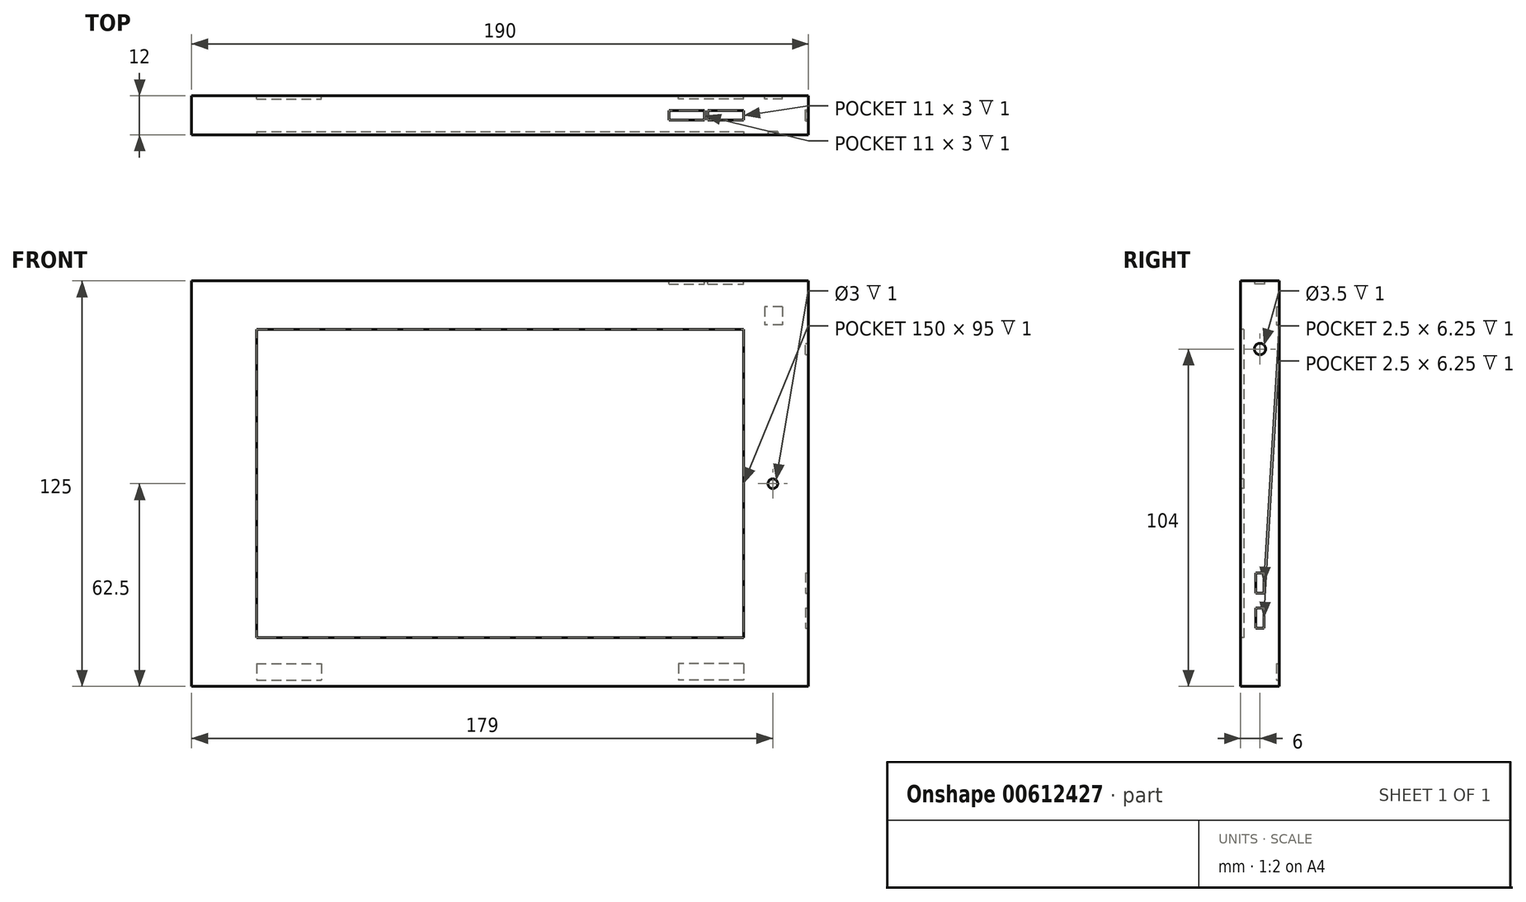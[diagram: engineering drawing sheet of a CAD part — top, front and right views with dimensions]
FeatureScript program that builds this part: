
annotation { "Feature Type Name" : "Feature", "Feature Type Description" : "" }
export const myFeature = defineFeature(function(context is Context, id is Id, definition is map)
    precondition{}
    {
        {
            var Q0;
            Q0=qCreatedBy(makeId("Right.planeOp"),FACE);
            var sketch = newSketch(context, id + "F0", { "sketchPlane" : qUnion([Q0])});
            skLineSegment(sketch, "E0.bottom", {"start": v(-7.75, 65) * mm, "end": v(7.75, 65) * mm});
            skLineSegment(sketch, "E0.top", {"start": v(-7.75, -65) * mm, "end": v(7.75, -65) * mm});
            skLineSegment(sketch, "E0.left", {"start": v(-7.75, 65) * mm, "end": v(-7.75, -65) * mm});
            skLineSegment(sketch, "E0.right", {"start": v(7.75, 65) * mm, "end": v(7.75, -65) * mm});
            skSolve(sketch);
        }
        {
            var Q0;
            Q0 = qSketchRegion(id + "F0", true);
            extrude(context, id + "F1", {"entities" : qUnion([Q0]), "endBound" : BoundingType.SYMMETRIC, "depth" : 200 * mm, "offsetDistance" : 25 * mm});
        }
        {
            var Q0;
            Q0=qCreatedBy(makeId("Right.planeOp"),FACE);
            var sketch = newSketch(context, id + "F2", { "sketchPlane" : qUnion([Q0])});
            skLineSegment(sketch, "E1.bottom", {"start": v(-6, 62.5) * mm, "end": v(6, 62.5) * mm});
            skLineSegment(sketch, "E1.top", {"start": v(-6, -62.5) * mm, "end": v(6, -62.5) * mm});
            skLineSegment(sketch, "E1.left", {"start": v(-6, 62.5) * mm, "end": v(-6, -62.5) * mm});
            skLineSegment(sketch, "E1.right", {"start": v(6, 62.5) * mm, "end": v(6, -62.5) * mm});
            skSolve(sketch);
        }
        {
            var Q0;
            Q0 = qSketchRegion(id + "F2", true);
            extrude(context, id + "F3", {"entities" : qUnion([Q0]), "endBound" : BoundingType.SYMMETRIC, "depth" : 190 * mm, "offsetDistance" : 25 * mm});
        }
        {
            var Q0;
            Q0=makeQuery(id+"F3.opExtrude","SWEPT_FACE",FACE,{"disambiguationData":[OSD([sQuery(id+"F2.wireOp",EDGE,"E1.right")])]});
            var sketch = newSketch(context, id + "F4", { "sketchPlane" : qUnion([Q0])});
            skLineSegment(sketch, "E2.bottom", {"start": v(-75, -55.5) * mm, "end": v(-55, -55.5) * mm});
            skLineSegment(sketch, "E2.top", {"start": v(-75, -60.5) * mm, "end": v(-55, -60.5) * mm});
            skLineSegment(sketch, "E2.left", {"start": v(-75, -55.5) * mm, "end": v(-75, -60.5) * mm});
            skLineSegment(sketch, "E2.right", {"start": v(-55, -55.5) * mm, "end": v(-55, -60.5) * mm});
            skLineSegment(sketch, "E3.bottom", {"start": v(75, -55.5) * mm, "end": v(55, -55.5) * mm});
            skLineSegment(sketch, "E3.top", {"start": v(75, -60.5) * mm, "end": v(55, -60.5) * mm});
            skLineSegment(sketch, "E3.left", {"start": v(75, -55.5) * mm, "end": v(75, -60.5) * mm});
            skLineSegment(sketch, "E3.right", {"start": v(55, -55.5) * mm, "end": v(55, -60.5) * mm});
            skLineSegment(sketch, "E4.bottom", {"start": v(-87, 54.5) * mm, "end": v(-81.5, 54.5) * mm});
            skLineSegment(sketch, "E4.top", {"start": v(-87, 49) * mm, "end": v(-81.5, 49) * mm});
            skLineSegment(sketch, "E4.left", {"start": v(-87, 54.5) * mm, "end": v(-87, 49) * mm});
            skLineSegment(sketch, "E4.right", {"start": v(-81.5, 54.5) * mm, "end": v(-81.5, 49) * mm});
            skSolve(sketch);
        }
        {
            var Q0;
            Q0 = qSketchRegion(id + "F4", true);
            extrude(context, id + "F5", {"entities" : qUnion([Q0]), "operationType" : NewBodyOperationType.REMOVE, "oppositeDirection" : true, "depth" : 1 * mm, "offsetDistance" : 25 * mm});
        }
        {
            var Q0;
            Q0=makeQuery(id+"F3.opExtrude","CAP_FACE",FACE,{"disambiguationData":[OSD([sQuery(id+"F2.wireOp",EDGE,"E1.bottom"),sQuery(id+"F2.wireOp",EDGE,"E1.top"),sQuery(id+"F2.wireOp",EDGE,"E1.left"),sQuery(id+"F2.wireOp",EDGE,"E1.right")])],"isStart":false});
            var sketch = newSketch(context, id + "F6", { "sketchPlane" : qUnion([Q0])});
            skLineSegment(sketch, "E5.bottom", {"start": v(-1.25, -27.5) * mm, "end": v(1.25, -27.5) * mm});
            skLineSegment(sketch, "E5.top", {"start": v(-1.25, -33.75) * mm, "end": v(1.25, -33.75) * mm});
            skLineSegment(sketch, "E5.left", {"start": v(1.25, -27.5) * mm, "end": v(1.25, -33.75) * mm});
            skLineSegment(sketch, "E5.right", {"start": v(-1.25, -27.5) * mm, "end": v(-1.25, -33.75) * mm});
            skLineSegment(sketch, "E6.bottom", {"start": v(-1.25, -38.25) * mm, "end": v(1.25, -38.25) * mm});
            skLineSegment(sketch, "E6.top", {"start": v(-1.25, -44.5) * mm, "end": v(1.25, -44.5) * mm});
            skLineSegment(sketch, "E6.left", {"start": v(1.25, -38.25) * mm, "end": v(1.25, -44.5) * mm});
            skLineSegment(sketch, "E6.right", {"start": v(-1.25, -38.25) * mm, "end": v(-1.25, -44.5) * mm});
            skLineSegment(sketch, "E7", {"start": v(0, 62.5) * mm, "end": v(0, -62.5) * mm, "construction": true});
            skCircle(sketch, "E8", {"center": v(0, 41.5) * mm, "radius": 1.75 * mm});
            skSolve(sketch);
        }
        {
            var Q0;
            Q0 = qSketchRegion(id + "F6", true);
            extrude(context, id + "F7", {"entities" : qUnion([Q0]), "operationType" : NewBodyOperationType.REMOVE, "oppositeDirection" : true, "depth" : 1 * mm, "offsetDistance" : 25 * mm});
        }
        {
            var Q0;
            Q0=makeQuery(id+"F3.opExtrude","SWEPT_FACE",FACE,{"disambiguationData":[OSD([sQuery(id+"F2.wireOp",EDGE,"E1.bottom")])]});
            var sketch = newSketch(context, id + "F8", { "sketchPlane" : qUnion([Q0])});
            skLineSegment(sketch, "E9.bottom", {"start": v(52, 1.5) * mm, "end": v(63, 1.5) * mm});
            skLineSegment(sketch, "E9.top", {"start": v(52, -1.5) * mm, "end": v(63, -1.5) * mm});
            skLineSegment(sketch, "E9.left", {"start": v(52, 1.5) * mm, "end": v(52, -1.5) * mm});
            skLineSegment(sketch, "E9.right", {"start": v(63, 1.5) * mm, "end": v(63, -1.5) * mm});
            skLineSegment(sketch, "E10.bottom", {"start": v(64, 1.5) * mm, "end": v(75, 1.5) * mm});
            skLineSegment(sketch, "E10.top", {"start": v(64, -1.5) * mm, "end": v(75, -1.5) * mm});
            skLineSegment(sketch, "E10.left", {"start": v(64, 1.5) * mm, "end": v(64, -1.5) * mm});
            skLineSegment(sketch, "E10.right", {"start": v(75, 1.5) * mm, "end": v(75, -1.5) * mm});
            skSolve(sketch);
        }
        {
            var Q0;
            Q0 = qSketchRegion(id + "F8", true);
            extrude(context, id + "F9", {"entities" : qUnion([Q0]), "operationType" : NewBodyOperationType.REMOVE, "oppositeDirection" : true, "depth" : 1 * mm, "offsetDistance" : 25 * mm});
        }
        {
            var Q0;
            Q0=makeQuery(id+"F3.opExtrude","SWEPT_FACE",FACE,{"disambiguationData":[OSD([sQuery(id+"F2.wireOp",EDGE,"E1.left")])]});
            var sketch = newSketch(context, id + "F10", { "sketchPlane" : qUnion([Q0])});
            skLineSegment(sketch, "E11.bottom", {"start": v(-75, 47.5) * mm, "end": v(75, 47.5) * mm});
            skLineSegment(sketch, "E11.top", {"start": v(-75, -47.5) * mm, "end": v(75, -47.5) * mm});
            skLineSegment(sketch, "E11.left", {"start": v(-75, 47.5) * mm, "end": v(-75, -47.5) * mm});
            skLineSegment(sketch, "E11.right", {"start": v(75, 47.5) * mm, "end": v(75, -47.5) * mm});
            skCircle(sketch, "E12", {"center": v(84, 0) * mm, "radius": 1.5 * mm});
            skSolve(sketch);
        }
        {
            var Q0;
            Q0 = qSketchRegion(id + "F10", true);
            extrude(context, id + "F11", {"entities" : qUnion([Q0]), "operationType" : NewBodyOperationType.REMOVE, "oppositeDirection" : true, "depth" : 1 * mm, "offsetDistance" : 25 * mm});
        }
        {
            var Q0;
            Q0=makeQuery(id+"F1.opExtrude","SWEPT_BODY",BODY,{"disambiguationData":[OSD([sQuery(id+"F0.wireOp",EDGE,"E0.bottom"),sQuery(id+"F0.wireOp",EDGE,"E0.top"),sQuery(id+"F0.wireOp",EDGE,"E0.left"),sQuery(id+"F0.wireOp",EDGE,"E0.right")])]});
            deleteBodies(context, id + "F12", {"entities" : qUnion([Q0])});
        }
    });
